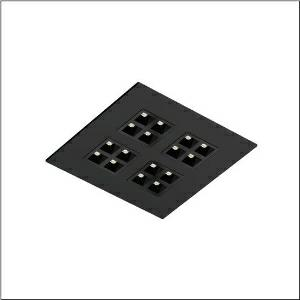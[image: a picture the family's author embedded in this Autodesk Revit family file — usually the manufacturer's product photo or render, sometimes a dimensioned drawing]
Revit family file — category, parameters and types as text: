
# Revit family: silica_r__31_square_51my6lds34ba_2ec9
name_source: partatom
category: Lighting Fixtures
units: mm (PartAtom-declared; Revit-internal decimal feet)

## family parameters
Cut with Voids When Loaded = No
Host = Face
Light Source = No
Part Type = Normal
Room Calculation Point = No
Round Connector Dimension = Use Diameter
Shared = No

## types (1)
- --- (1 x LED, 5980 lm, 38.5 W, 3000K)
    Apparent Load = 39 VA
    CIE Flux Codes = 82 100 100 100 100
    Color Rendering = 80
    Color Temperature = 3000K
    Default Elevation = 1800 mm
    Description = Silica® 31 Square, office luminaire, primary light control with lens, of PMMA, primary anti-glare with reflector, of PC, black, light emission: direct distribution, primary light characteristic: symmetric, installation type: lay-in mounting, LED, rated luminous flux: 4.650lm, luminous efficacy: 158lm/W, light colour: 830, colour temperature: 3000K, control gear: DALI 2, Multilumen, with terminal, 5-pole, mains connection: 220..240V, AC, 50/60Hz, rated input power: 29.4W, luminaire housing, of sheet steel, coated, jet black (RAL 9005), module: M600, length: 595mm, width: 595mm, height: 43mm, protection rating (complete): IP20, insulation class (complete): insulation class II (safety insulation), certification: CE, impact resistance: IK03, permissible operating ambient temperature: -20..+35°C, standard: EN 50419, packaging unit: 1 piece
    Height = 0 mm  [stored 0 ft]
    Lamp = 1 x LED
    Lamp Light Flux = 5980 lm
    Lamp Power = 38.5 W
    Lamp count = 1
    Length = 595 mm
    Luminous efficacy = 155 lm/W
    Manufacturer = Siteco
    ModVariant = No
    Model = 51MY6LDS34BA
    Mounting Place = Ceiling
    Mounting Type = Recessed
    Number of Poles = 1
    OnlyDefault = Yes
    Power Factor = 1
    Product Name = Silica® 31 Square
    Product group = office luminaire | ceiling recessed
    ProductGroupID = 401
    Protection Class = Protection class II
    Protection Degree = IP 20
    RLX_Detail_Level = 1
    RLX_Emergency_Light_Flux = 0 lm
    RLX_Emergency_Type = 0
    RLX_Emergency_Type_DB = No
    RlxData = <blob elided: 35465 chars, md5=a4982a5d>
    Socket = socket
    Standby Power = 0 W
    System Light Flux = 5980 lm
    System Power = 39 W
    Type Comments = factory setting: luminous flux: 100 % | (OFF | OFF | OFF | OFF) | 1050 mA
    Type Image = l_1313660.jpg
    URL = http://relux.com
    VarID = @adj_036138
    Voltage = 0 V
    Weight = 0.00 kg
    Width = 595 mm

note: [stored X ft] marks values corroborated as IEEE doubles in the binary element streams (Revit-internal decimal feet)

## geometry (parser evidence)
native form markers: Blend x4, Sweep x10
no freeform markers — native parametric forms only
